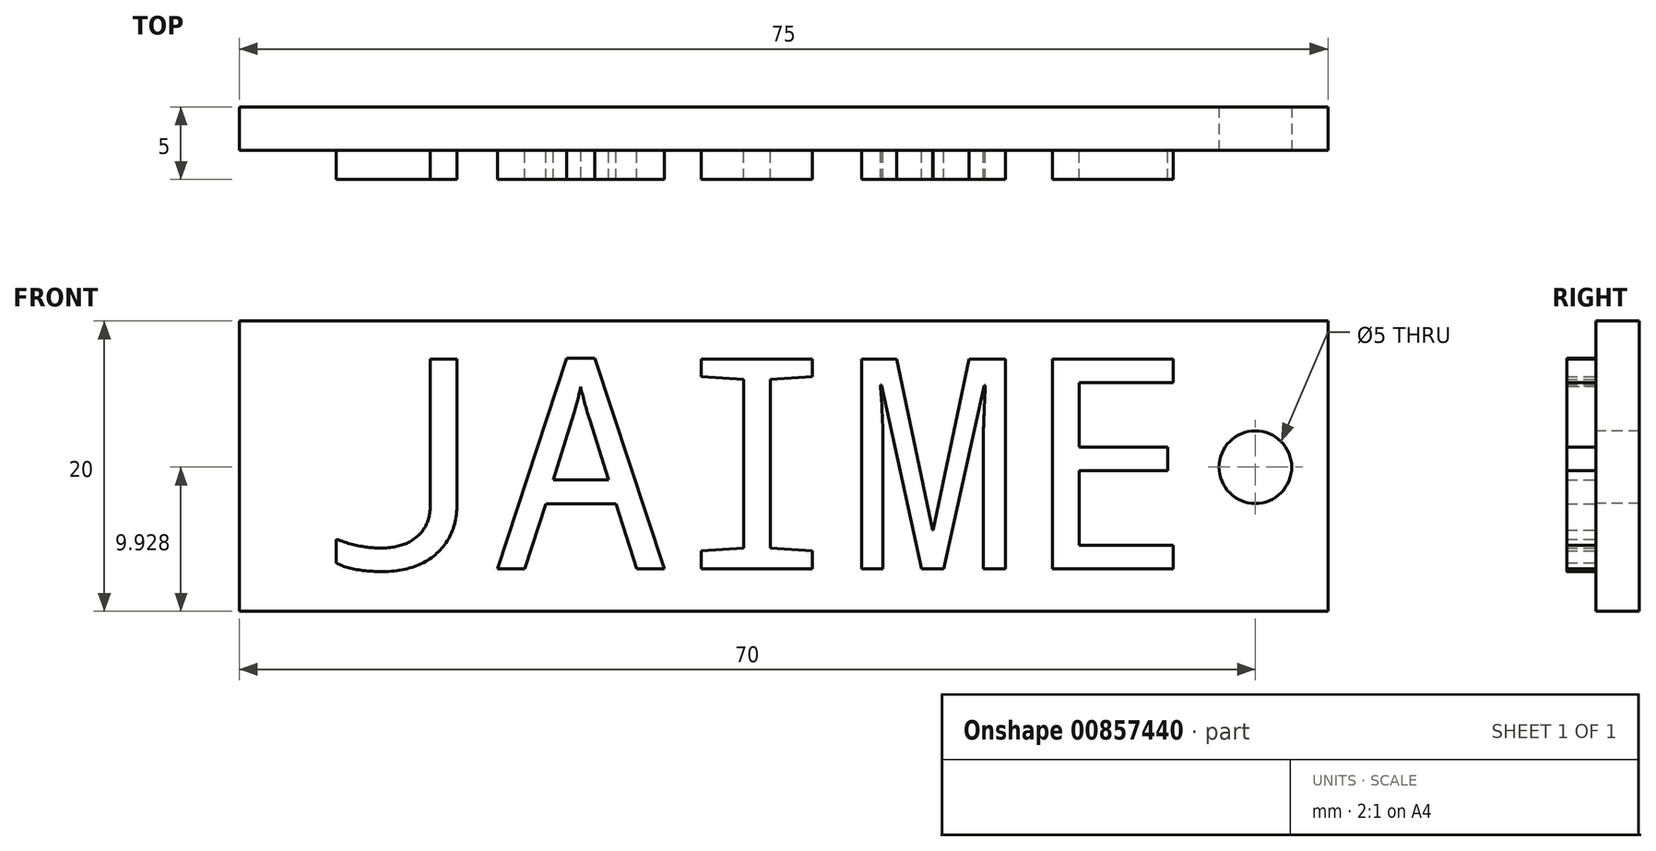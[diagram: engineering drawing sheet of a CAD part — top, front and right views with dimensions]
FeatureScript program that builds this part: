
annotation { "Feature Type Name" : "Feature", "Feature Type Description" : "" }
export const myFeature = defineFeature(function(context is Context, id is Id, definition is map)
    precondition{}
    {
        {
            var Q0;
            Q0=qCreatedBy(makeId("Front.planeOp"),FACE);
            var sketch = newSketch(context, id + "F0", { "sketchPlane" : qUnion([Q0])});
            skLineSegment(sketch, "E0.bottom", {"start": v(0, 0) * mm, "end": v(75, 0) * mm});
            skLineSegment(sketch, "E0.top", {"start": v(0, -20) * mm, "end": v(75, -20) * mm});
            skLineSegment(sketch, "E0.left", {"start": v(0, 0) * mm, "end": v(0, -20) * mm});
            skLineSegment(sketch, "E0.right", {"start": v(75, 0) * mm, "end": v(75, -20) * mm});
            skPoint(sketch, "E1.centerSnap0", {"position": v(75, -10) * mm});
            skCircle(sketch, "E2", {"center": v(70, -10.07) * mm, "radius": 2.5 * mm});
            skSolve(sketch);
        }
        {
            var Q0;
            Q0=makeQuery(id+"F0.imprint","IMPRINT",FACE,{"disambiguationData":[TD([[makeQuery(id+"F0.imprint","IMPRINT",EDGE,{"derivedFrom":sQuery(id+"F0.wireOp",EDGE,"E0.bottom")}),-1.0]])]});
            var sketch = newSketch(context, id + "F1", { "sketchPlane" : qUnion([Q0])});
            skSolve(sketch);
        }
        {
            var Q0;
            Q0=makeQuery(id+"F1.imprint","IMPRINT",FACE,{"disambiguationData":[TD([[makeQuery(id+"F1.imprint","IMPRINT",EDGE,{"derivedFrom":makeQuery(id+"F0.imprint","IMPRINT",EDGE,{"derivedFrom":sQuery(id+"F0.wireOp",EDGE,"E0.bottom")})}),-1.0]])]});
            extrude(context, id + "F2", {"entities" : qUnion([Q0]), "oppositeDirection" : true, "depth" : 3 * mm, "offsetDistance" : 25 * mm});
        }
        {
            var Q0;
            Q0=makeQuery(id+"F0.imprint","IMPRINT",FACE,{"disambiguationData":[TD([[makeQuery(id+"F0.imprint","IMPRINT",EDGE,{"derivedFrom":sQuery(id+"F0.wireOp",EDGE,"E0.bottom")}),-1.0]])]});
            var sketch = newSketch(context, id + "F3", { "sketchPlane" : qUnion([Q0])});
            skText(sketch, "E3", { "text": "JAIME", "fontName": "DroidSansMono.ttf"});
            const initialGuessF3  = {"E3": [0.00534, -0.01706, 1, 0, 0.01456]};
            skSetInitialGuess(sketch, initialGuessF3);
            skSolve(sketch);
        }
        {
            var Q0;
            Q0 = qSketchRegion(id + "F3", true);
            extrude(context, id + "F4", {"entities" : qUnion([Q0]), "operationType" : NewBodyOperationType.ADD, "depth" : 2 * mm, "offsetDistance" : 25 * mm});
        }
    });
